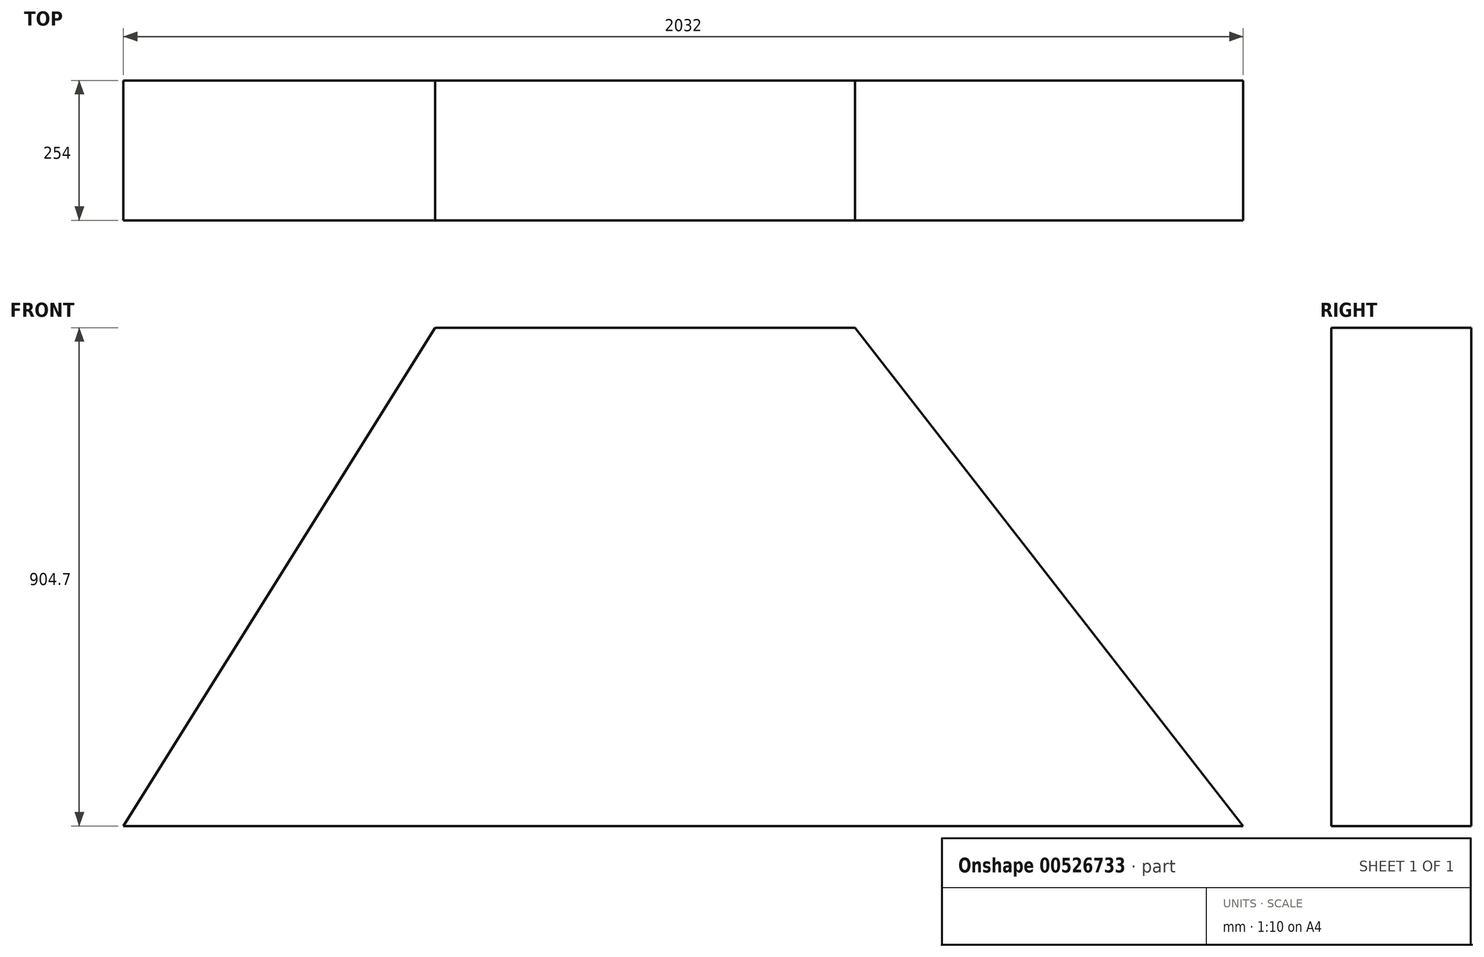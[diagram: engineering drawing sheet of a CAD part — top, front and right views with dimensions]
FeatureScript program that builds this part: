
annotation { "Feature Type Name" : "Feature", "Feature Type Description" : "" }
export const myFeature = defineFeature(function(context is Context, id is Id, definition is map)
    precondition{}
    {
        {
            var Q0;
            Q0=qCreatedBy(makeId("Front.planeOp"),FACE);
            var sketch = newSketch(context, id + "F0", { "sketchPlane" : qUnion([Q0])});
            skLineSegment(sketch, "E0", {"start": v(0, 0) * mm, "end": v(565.32, 904.7) * mm});
            skLineSegment(sketch, "E1", {"start": v(565.32, 904.7) * mm, "end": v(1327.32, 904.7) * mm});
            skLineSegment(sketch, "E2", {"start": v(1327.32, 904.7) * mm, "end": v(2032, 0) * mm});
            skLineSegment(sketch, "E3", {"start": v(2032, 0) * mm, "end": v(0, 0) * mm});
            skSolve(sketch);
        }
        {
            var Q0;
            Q0=makeQuery(id+"F0.imprint","IMPRINT",FACE,{"disambiguationData":[TD([[makeQuery(id+"F0.imprint","IMPRINT",EDGE,{"derivedFrom":sQuery(id+"F0.wireOp",EDGE,"E0")}),-1.0]])]});
            extrude(context, id + "F1", {"entities" : qUnion([Q0]), "depth" : 254 * mm, "offsetDistance" : 25.4 * mm});
        }
    });
